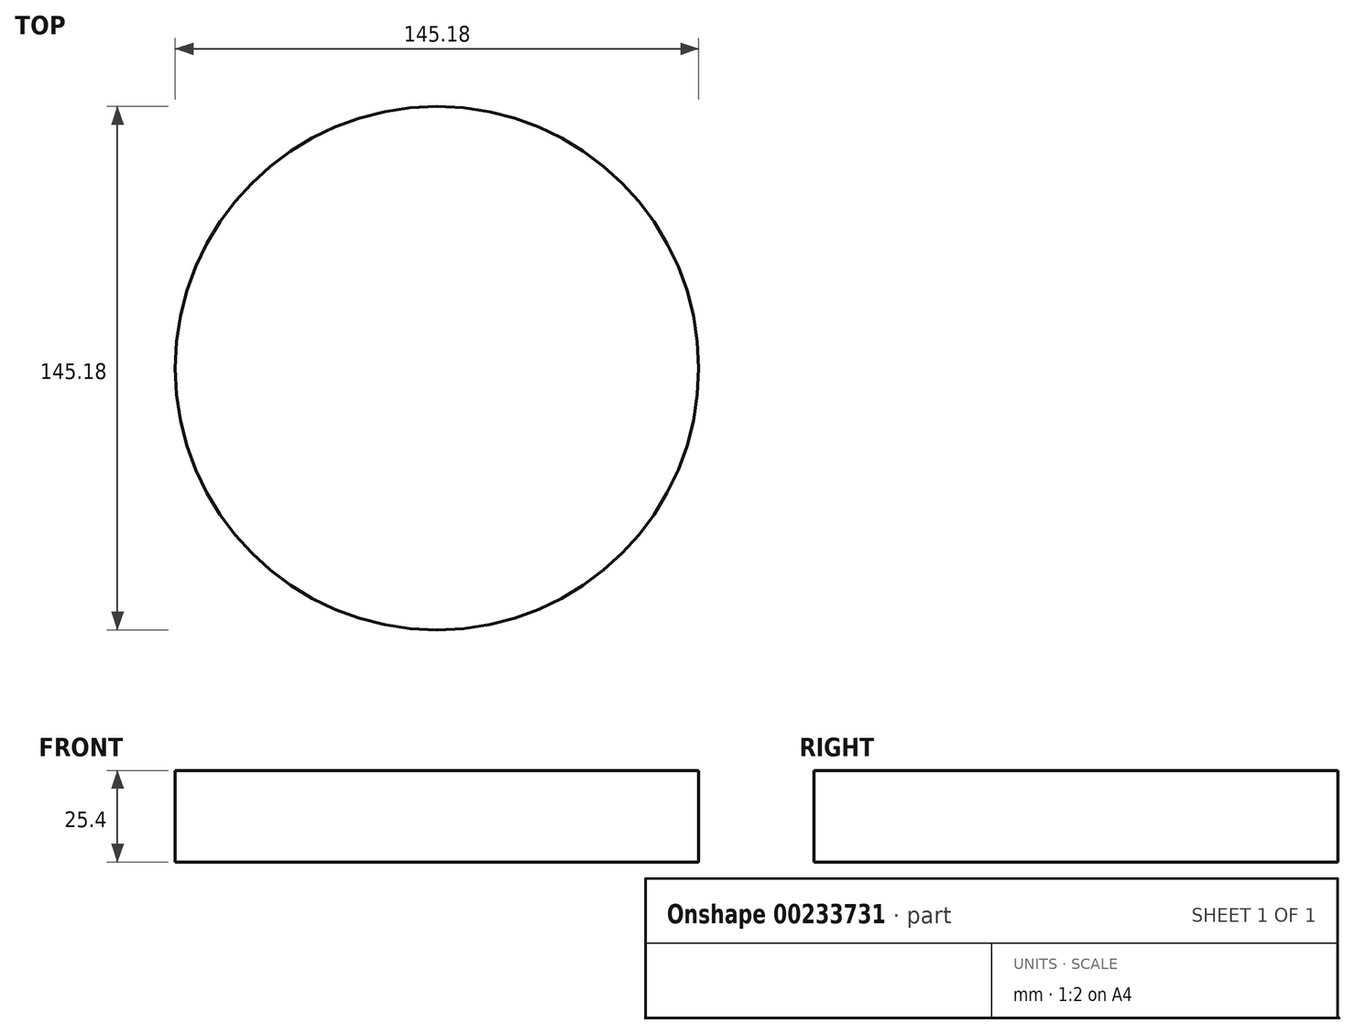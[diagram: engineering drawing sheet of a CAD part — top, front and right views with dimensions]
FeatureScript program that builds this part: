
annotation { "Feature Type Name" : "Feature", "Feature Type Description" : "" }
export const myFeature = defineFeature(function(context is Context, id is Id, definition is map)
    precondition{}
    {
        {
            var Q0;
            Q0=qCreatedBy(makeId("Top.planeOp"),FACE);
            var sketch = newSketch(context, id + "F2", { "sketchPlane" : qUnion([Q0])});
            skCircle(sketch, "E0", {"center": v(-37.9, 73.14) * mm, "radius": 72.6 * mm});
            skSolve(sketch);
        }
        {
            var Q0;
            Q0 = qSketchRegion(id + "F2", true);
            extrude(context, id + "F0", {"entities" : qUnion([Q0]), "depth" : 25.4 * mm});
        }
    });
